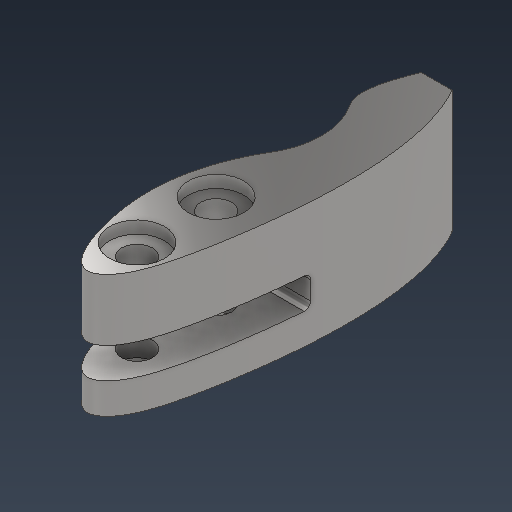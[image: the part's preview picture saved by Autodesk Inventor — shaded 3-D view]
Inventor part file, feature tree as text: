
AUTODESK INVENTOR PART (.ipt)
format: ipt  version: 2021 (Build 250183000, 183)  size: 217,088 bytes
history: native  units: mm
features: sketch x5, extrude x4, hole x1, plane x1, fillet x1, projected_geometry x1
ambient origin geometry x8: Origin, YZ Plane, XZ Plane, XY Plane, X Axis, Y Axis, Z Axis, Center Point
bodies: Solid1 (feature_tree)
feature tree (13):
  extrude  "Extrusion1"  TaperAngle=0.0deg  [1 undecoded]
  hole  "Hole1"  [1 undecoded]
  plane  "Work Plane1"
  extrude  "Extrusion2"  Depth=2.0mm
  fillet  "Fillet1"  Radius=2.0mm
  extrude  "Extrusion3"  Depth=5.0mm
  extrude  "Extrusion4"  Depth=12.133mm
  sketch  "Sketch1"  dims[d0=47.112mm d1=0.0mm]
  sketch  "Sketch2"  dims[d2=12.113mm d3=30.0mm]
  sketch  "Sketch3"  dims[d4=12.887mm d5=12.113mm d6=2.0mm]
  projected_geometry  "Projected Loop1"
  sketch  "Sketch4"  dims[d7=2.0mm d8=5.0mm]
  sketch  "Sketch5"  dims[d9=20.0mm d10=0.0mm d11=12.133mm d12=0.0mm d13=12.877mm d14=5.0mm d15=6.0mm d16=4.0mm d17=2.0mm d18=90.0deg d19=8.0mm d20=20.594885mm d22=5.0mm d23=20.0mm d24=10.0mm d25=50.0mm d26=10.0mm d27=0.0mm d28=1.0mm d29=5.0mm d30=4.5mm d31=2.0mm d32=2.0mm d33=2.0mm d34=0.0mm d35=2.0mm d36=2.0mm d37=2.0mm d38=0.0mm]
note: 2 required parameter values undecoded (feature->parameter linkage not recoverable at this tier; creation-order binding heuristic only, values carry confidence <= 0.55)
